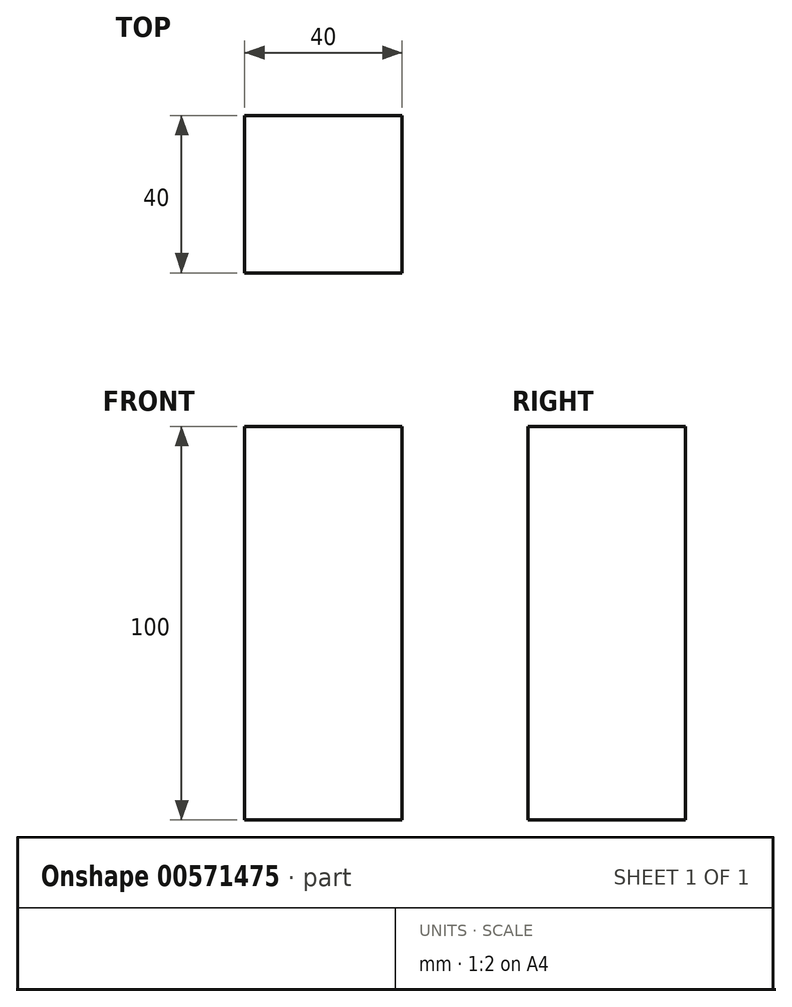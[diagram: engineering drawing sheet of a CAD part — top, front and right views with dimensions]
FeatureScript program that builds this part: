
annotation { "Feature Type Name" : "Feature", "Feature Type Description" : "" }
export const myFeature = defineFeature(function(context is Context, id is Id, definition is map)
    precondition{}
    {
        {
            var Q0;
            Q0=qCreatedBy(makeId("Top.planeOp"),FACE);
            var sketch = newSketch(context, id + "F0", { "sketchPlane" : qUnion([Q0])});
            skLineSegment(sketch, "E0.bottom", {"start": v(-20, 20) * mm, "end": v(20, 20) * mm});
            skLineSegment(sketch, "E0.top", {"start": v(-20, -20) * mm, "end": v(20, -20) * mm});
            skLineSegment(sketch, "E0.left", {"start": v(-20, 20) * mm, "end": v(-20, -20) * mm});
            skLineSegment(sketch, "E0.right", {"start": v(20, 20) * mm, "end": v(20, -20) * mm});
            skSolve(sketch);
        }
        {
            var Q0;
            Q0 = qSketchRegion(id + "F0", true);
            extrude(context, id + "F1", {"entities" : qUnion([Q0]), "depth" : 100 * mm, "offsetDistance" : 25 * mm});
        }
    });
